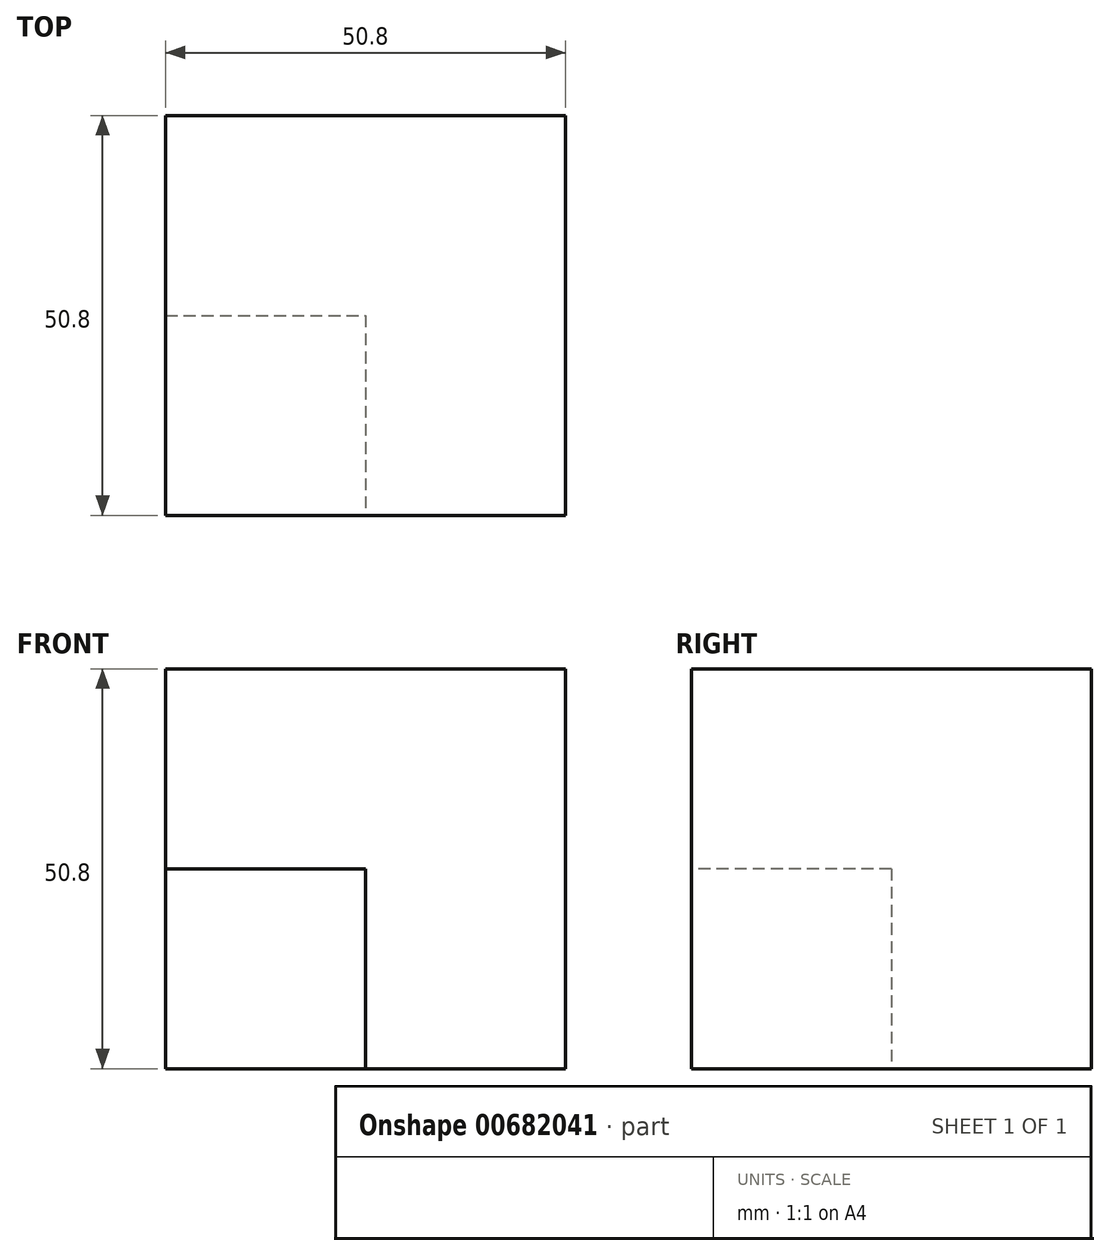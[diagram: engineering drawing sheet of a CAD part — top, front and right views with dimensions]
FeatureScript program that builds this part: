
annotation { "Feature Type Name" : "Feature", "Feature Type Description" : "" }
export const myFeature = defineFeature(function(context is Context, id is Id, definition is map)
    precondition{}
    {
        {
            var Q0;
            Q0=qCreatedBy(makeId("Front.planeOp"),FACE);
            var sketch = newSketch(context, id + "F0", { "sketchPlane" : qUnion([Q0])});
            skLineSegment(sketch, "E0", {"start": v(-50.8, 50.8) * mm, "end": v(-50.8, 0) * mm});
            skLineSegment(sketch, "E1", {"start": v(-50.8, 0) * mm, "end": v(0, 0) * mm});
            skLineSegment(sketch, "E2", {"start": v(-50.8, 50.8) * mm, "end": v(0, 50.8) * mm});
            skLineSegment(sketch, "E3", {"start": v(0, 50.8) * mm, "end": v(0, 0) * mm});
            skSolve(sketch);
        }
        {
            var Q0;
            Q0=makeQuery(id+"F0.imprint","IMPRINT",FACE,{"disambiguationData":[TD([[makeQuery(id+"F0.imprint","IMPRINT",EDGE,{"derivedFrom":sQuery(id+"F0.wireOp",EDGE,"E0")}),1.0]])]});
            extrude(context, id + "F1", {"entities" : qUnion([Q0]), "depth" : 50.8 * mm, "offsetDistance" : 25.4 * mm});
        }
        {
            var Q0;
            Q0=makeQuery(id+"F1.opExtrude","CAP_FACE",FACE,{"disambiguationData":[OSD([sQuery(id+"F0.wireOp",EDGE,"E0"),sQuery(id+"F0.wireOp",EDGE,"E1"),sQuery(id+"F0.wireOp",EDGE,"E2"),sQuery(id+"F0.wireOp",EDGE,"E3")])],"isStart":false});
            var sketch = newSketch(context, id + "F2", { "sketchPlane" : qUnion([Q0])});
            skLineSegment(sketch, "E4", {"start": v(-50.8, 25.4) * mm, "end": v(-25.4, 25.4) * mm});
            skLineSegment(sketch, "E5", {"start": v(-25.4, 25.4) * mm, "end": v(-25.4, 0) * mm});
            skLineSegment(sketch, "E6", {"start": v(-50.8, 25.4) * mm, "end": v(-50.8, 0) * mm});
            skLineSegment(sketch, "E7", {"start": v(-50.8, 0) * mm, "end": v(-25.4, 0) * mm});
            skSolve(sketch);
        }
        {
            var Q0;
            Q0 = qSketchRegion(id + "F2", true);
            extrude(context, id + "F3", {"entities" : qUnion([Q0]), "operationType" : NewBodyOperationType.REMOVE, "oppositeDirection" : true, "depth" : 25.4 * mm, "offsetDistance" : 25.4 * mm});
        }
    });
